# Revit family: HL_Переходник_HL9_1
name_source: partatom
category: Pipe Fittings
revit_build: Autodesk Revit 2016 (Build: 20150220_1215(x64)
units: mm (PartAtom-declared; Revit-internal decimal feet)

## family parameters
Always vertical = Yes
Cut with Voids When Loaded = No
OmniClass Number = 23.60.30.11.14
OmniClass Title = Pipework Fittings
Part Type = Transition
Round Connector Dimension = Use Diameter
Shared = No
Work Plane-Based = No

## types (2) — shared parameters
K Coefficient Table = Reducer/Coupling/Union/Increaser
Loss Method = K Coefficient from Table
Manufacturer = HL Hutterer & Lechner GmbH
URL = http://www.hutterer-lechner.com
МАТЕРИАЛ = PP
материал = Plactic - White

## per-type parameters (varying)
| type | Description | EAN | Keynote | L | Model | Type Comments | ВЕС | РАЗМЕР |
| HL9_7_1 | Переходник DN75/110 ПП/ПВХ на чугун/свинец | 9003076929719 | HL9/7/1 | 138 mm | HL9/7/1 | Переходник DN75/110 ПП/ПВХ на чугун/свинец | 0,307 kg | DN75/110 |
| HL9_50_1 | Переходник DN50/110 ПП/ПВХ на чугун/свинец | 9003076929511 | HL9/50/1 | 148 mm | HL9/50/1 | Переходник DN50/100 ПП/ПВХ на чугун/свинец | 0,295 kg | DN50/110 |

note: column(s) folded — value = type name in every type: Lookup Table Name

## geometry (parser evidence)
native form markers: Sweep x2
no freeform markers — native parametric forms only
